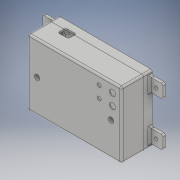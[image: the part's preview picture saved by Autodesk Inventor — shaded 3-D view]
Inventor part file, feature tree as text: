
AUTODESK INVENTOR PART (.ipt)
format: ipt  version: 2019 (Build 230136000, 136)  size: 466,944 bytes
history: native  units: mm
features: other x12, sketch x12, extrude x10, reference x6, fillet x3, projected_geometry x2, shell x1, split x1, hole x1, chamfer x1
ambient origin geometry x8: Origin, YZ Plane, XZ Plane, XY Plane, X Axis, Y Axis, Z Axis, Center Point
bodies: Solid1 (feature_tree)
feature tree (49):
  extrude  "Extrusion1"  Depth=75.0mm
  shell  "Shell1"  Thickness=35.0mm
  fillet  "Fillet2"  Radius=2.0mm
  extrude  "Extrusion10"  Depth=8.0mm
  extrude  "Extrusion11"  Depth=15.0mm
  fillet  "Fillet4"  Radius=15.0mm
  split  "Split1"
  extrude  "Extrusion2"  Depth=5.0mm
  extrude  "Extrusion3"  Depth=3.0mm TaperAngle=0.0deg
  fillet  "Fillet1"  Radius=2.0mm
  other  "Lip1"
  other  "Lip2"
  extrude  "Extrusion4"  Depth=1.0mm
  hole  "Hole1"  [1 undecoded]
  extrude  "Extrusion5"  Depth=8.0mm
  extrude  "Extrusion6"  Depth=23.5mm TaperAngle=0.0deg
  extrude  "Extrusion7"  Depth=5.5mm
  extrude  "Extrusion8"  Depth=3.0mm TaperAngle=0.0deg
  chamfer  "Chamfer1"  Distance=2.0mm
  sketch  "Sketch1"  dims[d0=106.0mm d1=75.0mm d2=35.0mm d3=0.0mm d4=2.0mm]
  sketch  "Sketch2"  dims[d5=9.0mm d6=8.0mm]
  sketch  "Sketch3"  dims[d7=5.0mm d8=0.0mm d9=15.0mm d10=15.0mm]
  reference  "Reference1"
  reference  "Reference2"
  reference  "Reference3"
  reference  "Reference4"
  sketch  "Sketch4"  dims[d11=5.0mm d12=5.0mm]
  projected_geometry  "Projected Loop1"
  sketch  "Sketch5"  dims[d13=4.0mm d14=3.0mm d15=0.0mm d16=2.0mm]
  sketch  "Sketch6"  dims[d17=2.0mm]
  sketch  "Sketch7"  dims[d18=1.0mm d19=1.0mm d20=0.0mm d21=0.0mm d22=0.0mm d23=0.0mm]
  projected_geometry  "Projected Loop2"
  sketch  "Sketch8"  dims[d24=1.0mm d25=1.0mm d26=0.0mm d27=0.0mm d28=0.0mm d29=0.0mm d30=2.6mm]
  sketch  "Sketch9"  dims[d31=2.6mm d32=2.6mm]
  sketch  "Sketch10"  dims[d33=2.6mm d34=8.0mm d35=2.6mm]
  reference  "Reference5"
  reference  "Reference6"
  sketch  "Sketch12"  dims[d36=8.0mm d37=2.6mm]
  sketch  "Sketch13"  dims[d38=3.3mm d39=6.0mm d40=6.0mm d41=21.5mm d42=90.0deg d43=36.25mm d44=0.0mm d45=23.5mm d46=0.0mm d47=5.5mm d48=3.0mm d49=0.0mm d50=2.0mm d51=6.8mm d52=10.0mm d53=10.0mm d54=13.0mm d55=4.3mm d56=15.0mm d57=3.0mm d58=0.0mm d59=11.0mm d60=6.0mm d61=1.0mm d62=0.0mm d63=11.0mm d64=11.0mm d65=30.0mm d66=28.0mm d67=5.1mm d68=0.0mm d69=7.0mm d74=16.0mm d75=12.0mm d76=17.0mm d77=8.0mm d78=10.0mm d79=0.0mm d81=8.0mm d82=17.0mm d83=29.0mm d84=30.0mm d85=10.0mm d86=0.0mm d87=2.0mm d88=8.0mm d89=12.0mm d90=24.375mm d91=18.504mm d92=1.0mm d93=3.5mm d94=2.0mm d95=45.0deg]
  other  "Top"
  other  "Bottom"
  parser-record x1  (decoder bookkeeping rows leaked as tree rows — omitted from the tree; the rows remain in map.json)
  other  "Enclosure Assembly.iam"
  other  "HexaWall-v1.1 v6:1"
  other  "Board:1"
  other  "Packages:1"
  other  "W237-102 (1):X1"
  other  "TB006-508-02P_Green - S:1"
  other  "W237-103:X3"
note: 1 required parameter value undecoded (feature->parameter linkage not recoverable at this tier; creation-order binding heuristic only, values carry confidence <= 0.55)
note: 1 file-system path scrubbed to <path> (originals preserved in map.json)
